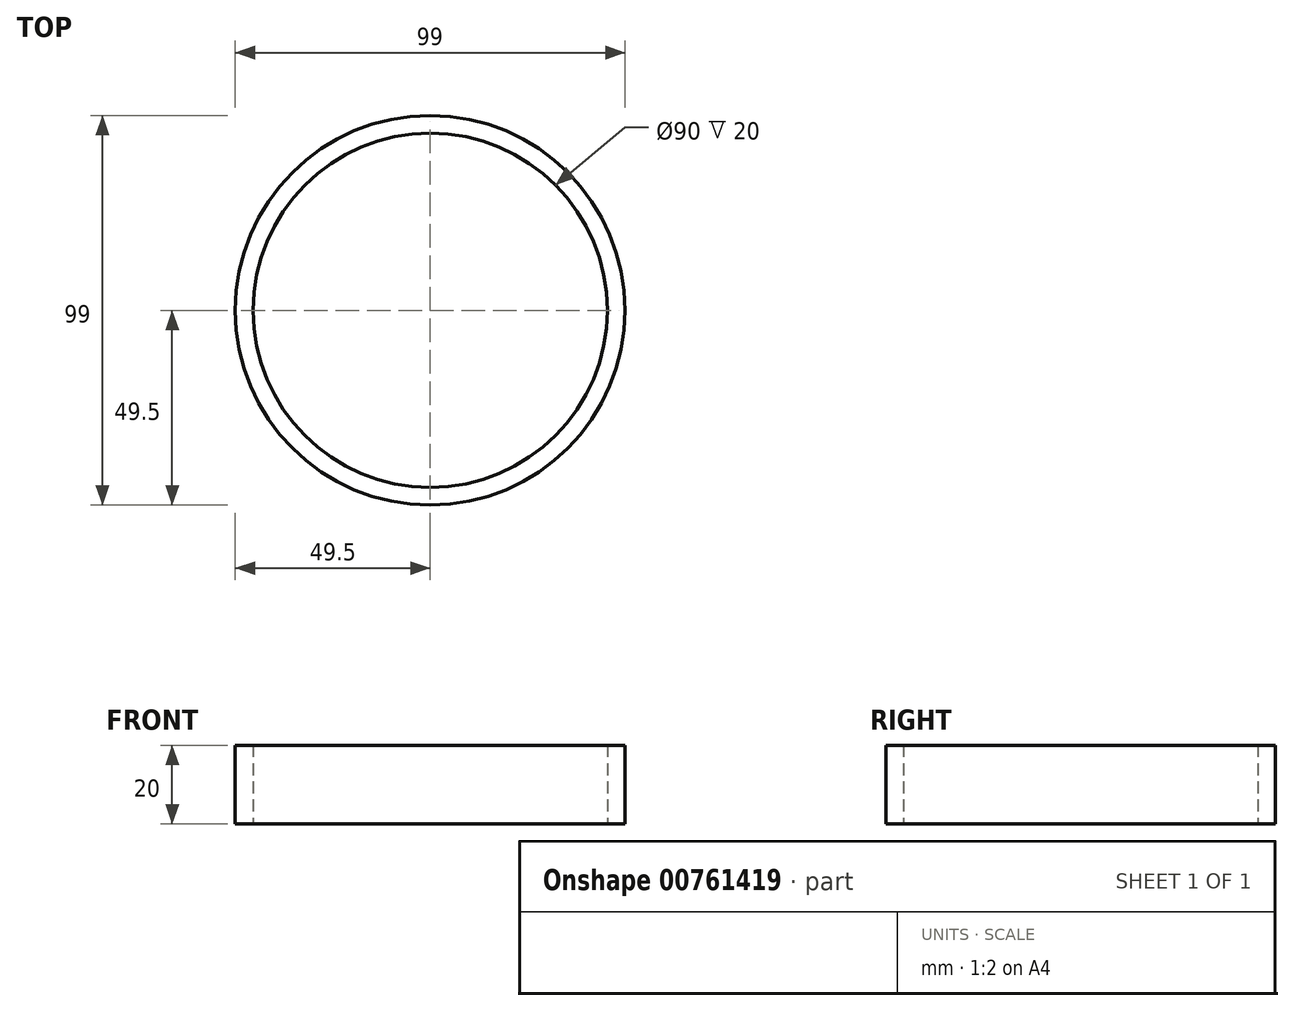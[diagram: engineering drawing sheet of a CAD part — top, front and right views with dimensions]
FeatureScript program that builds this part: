
annotation { "Feature Type Name" : "Feature", "Feature Type Description" : "" }
export const myFeature = defineFeature(function(context is Context, id is Id, definition is map)
    precondition{}
    {
        {
            var Q0;
            Q0=qCreatedBy(makeId("Top.planeOp"),FACE);
            var sketch = newSketch(context, id + "F0", { "sketchPlane" : qUnion([Q0])});
            skCircle(sketch, "E0", {"center": v(0, 0) * mm, "radius": 45 * mm});
            skCircle(sketch, "E1", {"center": v(0, 0) * mm, "radius": 49.5 * mm});
            skSolve(sketch);
        }
        {
            var Q0;
            Q0=makeQuery(id+"F0.imprint","IMPRINT",FACE,{"disambiguationData":[TD([[makeQuery(id+"F0.imprint","IMPRINT",EDGE,{"derivedFrom":sQuery(id+"F0.wireOp",EDGE,"E0")}),-1.0]])]});
            extrude(context, id + "F1", {"entities" : qUnion([Q0]), "depth" : 20 * mm, "offsetDistance" : 25 * mm});
        }
    });
